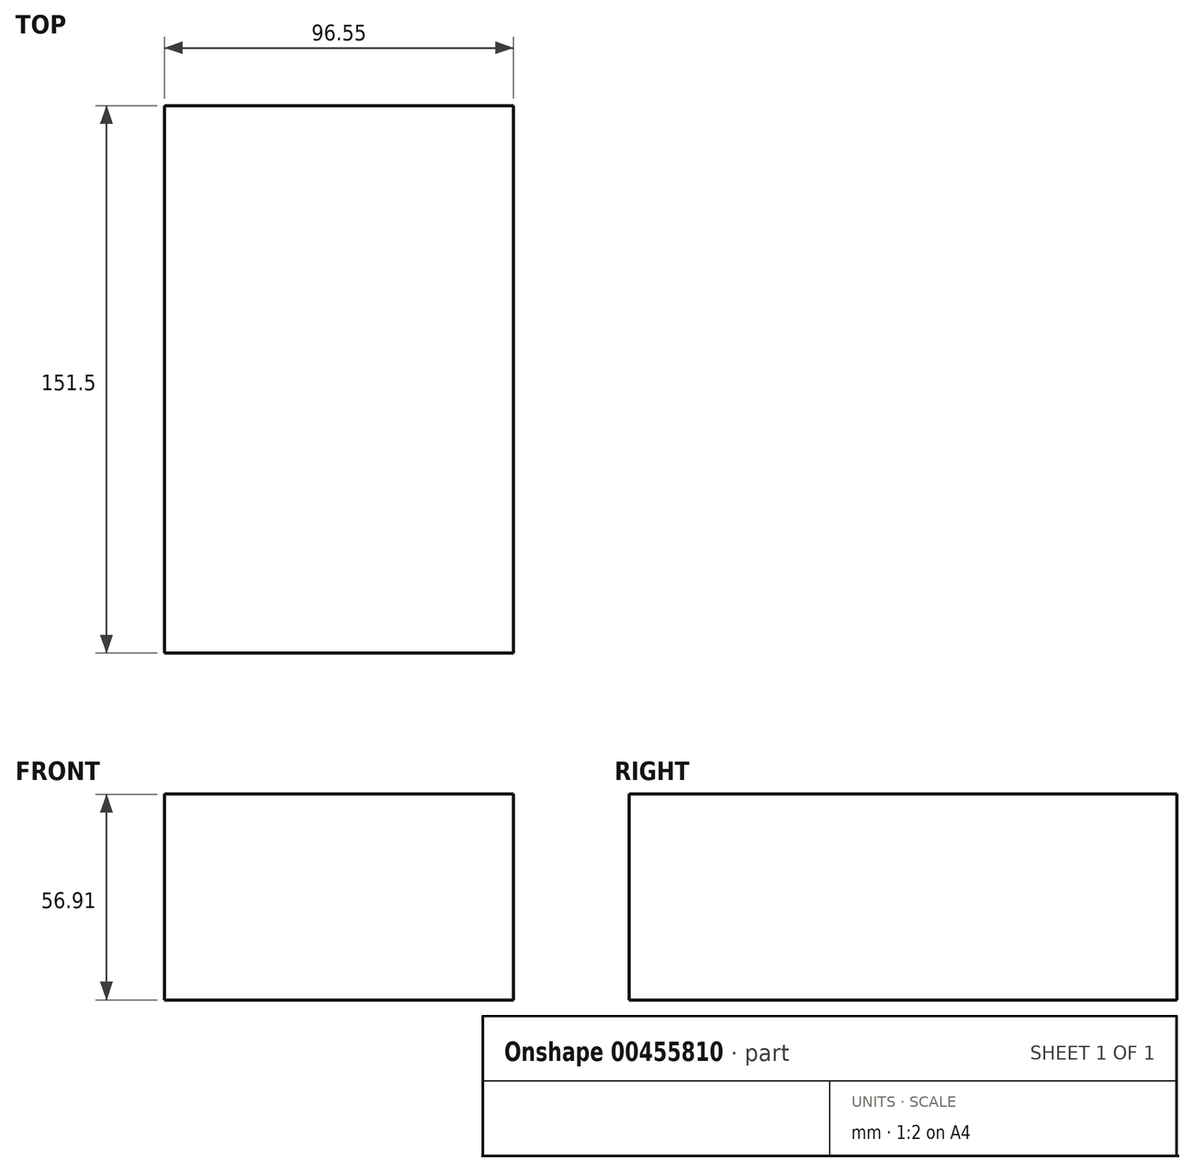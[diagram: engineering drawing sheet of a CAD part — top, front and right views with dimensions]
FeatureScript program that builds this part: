
annotation { "Feature Type Name" : "Feature", "Feature Type Description" : "" }
export const myFeature = defineFeature(function(context is Context, id is Id, definition is map)
    precondition{}
    {
        {
            var Q0;
            Q0=qCreatedBy(makeId("Top.planeOp"),FACE);
            var sketch = newSketch(context, id + "F0", { "sketchPlane" : qUnion([Q0])});
            skLineSegment(sketch, "E0.bottom", {"start": v(46.63, -74.61) * mm, "end": v(-49.92, -74.61) * mm});
            skLineSegment(sketch, "E0.top", {"start": v(46.63, 76.89) * mm, "end": v(-49.92, 76.89) * mm});
            skLineSegment(sketch, "E0.left", {"start": v(46.63, -74.61) * mm, "end": v(46.63, 76.89) * mm});
            skLineSegment(sketch, "E0.right", {"start": v(-49.92, -74.61) * mm, "end": v(-49.92, 76.89) * mm});
            skSolve(sketch);
        }
        {
            var Q0;
            Q0=makeQuery(id+"F0.imprint","IMPRINT",FACE,{"disambiguationData":[TD([[makeQuery(id+"F0.imprint","IMPRINT",EDGE,{"derivedFrom":sQuery(id+"F0.wireOp",EDGE,"E0.bottom")}),-1.0]])]});
            var Q1;
            Q1=sQuery(id+"F0.wireOp",EDGE,"E0.left");
            var Q2;
            Q2=sQuery(id+"F0.wireOp",EDGE,"E0.right");
            var Q3;
            Q3=sQuery(id+"F0.wireOp",EDGE,"E0.bottom");
            var Q4;
            Q4=sQuery(id+"F0.wireOp",EDGE,"E0.top");
            extrude(context, id + "F1", {"entities" : qUnion([Q0]), "bodyType" : ToolBodyType.SURFACE, "surfaceEntities" : qUnion([Q1, Q2, Q3, Q4]), "depth" : 1.18 * mm, "hasSecondDirection" : true, "secondDirectionOppositeDirection" : true, "secondDirectionDepth" : 55.73 * mm});
        }
    });
